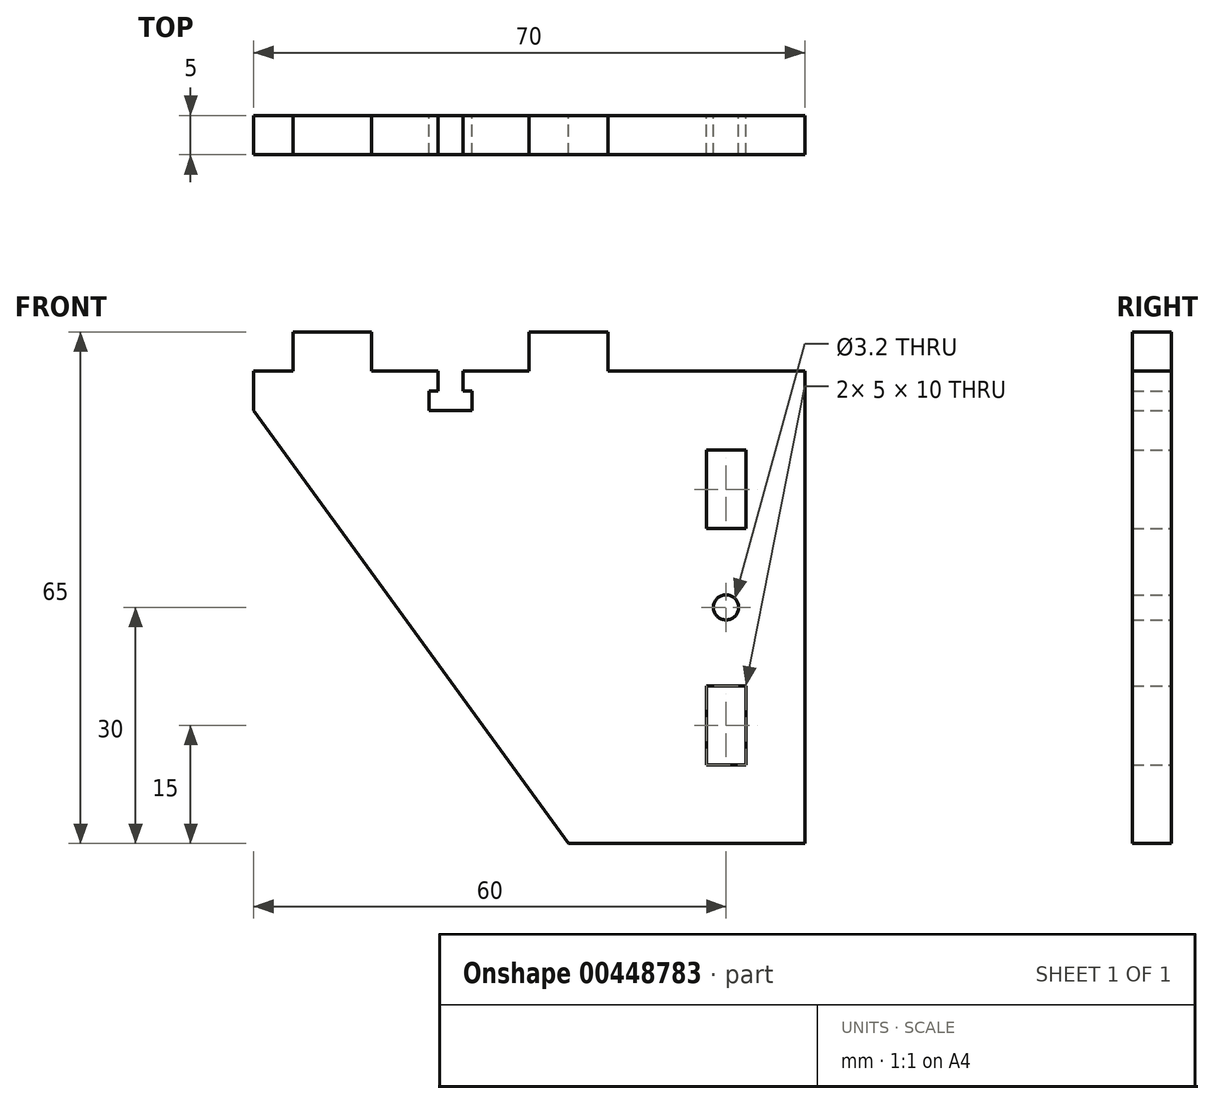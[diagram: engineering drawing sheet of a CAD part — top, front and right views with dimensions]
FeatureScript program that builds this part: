
annotation { "Feature Type Name" : "Feature", "Feature Type Description" : "" }
export const myFeature = defineFeature(function(context is Context, id is Id, definition is map)
    precondition{}
    {
        {
            assignVariable(context, id + "F0", {"name" : "thickness", "anyValue" : 5 * mm});
        }
        {
            var Q0;
            Q0=qCreatedBy(makeId("Front.planeOp"),FACE);
            var sketch = newSketch(context, id + "F1", { "sketchPlane" : qUnion([Q0])});
            skLineSegment(sketch, "E0", {"start": v(0, 0) * mm, "end": v(-30, 0) * mm});
            skLineSegment(sketch, "E1", {"start": v(-70, 60) * mm, "end": v(-65, 60) * mm});
            skLineSegment(sketch, "E2", {"start": v(0, 60) * mm, "end": v(0, 0) * mm});
            skLineSegment(sketch, "E3.bottom", {"start": v(-12.5, 10) * mm, "end": v(-7.5, 10) * mm});
            skLineSegment(sketch, "E3.top", {"start": v(-12.5, 20) * mm, "end": v(-7.5, 20) * mm});
            skLineSegment(sketch, "E3.left", {"start": v(-12.5, 10) * mm, "end": v(-12.5, 20) * mm});
            skLineSegment(sketch, "E3.right", {"start": v(-7.5, 10) * mm, "end": v(-7.5, 20) * mm});
            skLineSegment(sketch, "E4.bottom", {"start": v(-12.5, 40) * mm, "end": v(-7.5, 40) * mm});
            skLineSegment(sketch, "E4.top", {"start": v(-12.5, 50) * mm, "end": v(-7.5, 50) * mm});
            skLineSegment(sketch, "E4.left", {"start": v(-12.5, 40) * mm, "end": v(-12.5, 50) * mm});
            skLineSegment(sketch, "E4.right", {"start": v(-7.5, 40) * mm, "end": v(-7.5, 50) * mm});
            skCircle(sketch, "E5", {"center": v(-10, 30) * mm, "radius": 1.6 * mm});
            skPoint(sketch, "E5.centerSnap0", {"position": v(-10, 40) * mm});
            skPoint(sketch, "E5.centerSnap1", {"position": v(0, 30) * mm});
            skLineSegment(sketch, "E6", {"start": v(-65, 60) * mm, "end": v(-65, 65) * mm});
            skLineSegment(sketch, "E7", {"start": v(-65, 65) * mm, "end": v(-55, 65) * mm});
            skLineSegment(sketch, "E8", {"start": v(-55, 65) * mm, "end": v(-55, 60) * mm});
            skLineSegment(sketch, "E9", {"start": v(-35, 60) * mm, "end": v(-35, 65) * mm});
            skLineSegment(sketch, "E10", {"start": v(-35, 65) * mm, "end": v(-25, 65) * mm});
            skLineSegment(sketch, "E11", {"start": v(-25, 65) * mm, "end": v(-25, 60) * mm});
            skLineSegment(sketch, "E12", {"start": v(-46.6, 60) * mm, "end": v(-46.6, 57.5) * mm});
            skLineSegment(sketch, "E13", {"start": v(-46.6, 57.5) * mm, "end": v(-47.75, 57.5) * mm});
            skLineSegment(sketch, "E14", {"start": v(-47.75, 57.5) * mm, "end": v(-47.75, 55) * mm});
            skLineSegment(sketch, "E15", {"start": v(-47.75, 55) * mm, "end": v(-45, 55) * mm});
            skLineSegment(sketch, "E16", {"start": v(-45, 55) * mm, "end": v(-45, 60) * mm, "construction": true});
            skLineSegment(sketch, "E17.MirrorCS", {"start": v(-43.4, 57.5) * mm, "end": v(-42.25, 57.5) * mm});
            skLineSegment(sketch, "E18.MirrorCS", {"start": v(-42.25, 57.5) * mm, "end": v(-42.25, 55) * mm});
            skLineSegment(sketch, "E19.MirrorCS", {"start": v(-43.4, 60) * mm, "end": v(-43.4, 57.5) * mm});
            skLineSegment(sketch, "E20.MirrorCS", {"start": v(-42.25, 55) * mm, "end": v(-45, 55) * mm});
            skLineSegment(sketch, "E21.trimOffspring", {"start": v(-43.4, 60) * mm, "end": v(-35, 60) * mm});
            skLineSegment(sketch, "E22", {"start": v(-70, 60) * mm, "end": v(-70, 55) * mm});
            skLineSegment(sketch, "E23", {"start": v(-70, 55) * mm, "end": v(-30, 0) * mm});
            skLineSegment(sketch, "E24.trimOffspring", {"start": v(-25, 60) * mm, "end": v(0, 60) * mm});
            skLineSegment(sketch, "E25.trimOffspring", {"start": v(-55, 60) * mm, "end": v(-46.6, 60) * mm});
            skSolve(sketch);
        }
        {
            var Q0;
            Q0=qSketchRegion(id+"F1",true);
            extrude(context, id + "F2", {"entities" : qUnion([Q0]), "depth" : getVariable(context, 'thickness')});
        }
    });
